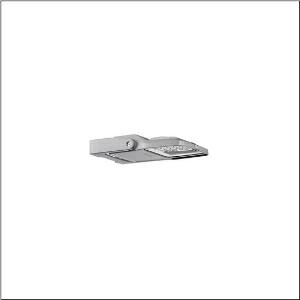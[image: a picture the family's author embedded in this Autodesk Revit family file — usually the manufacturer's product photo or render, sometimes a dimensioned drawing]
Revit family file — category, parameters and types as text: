
# Revit family: floodlight_fl_21_iq_micro___pl52_5xa7761a4d2a_29c7
name_source: partatom
category: Lighting Fixtures
units: mm (PartAtom-declared; Revit-internal decimal feet)

## family parameters
Cut with Voids When Loaded = No
Host = Face
Light Source = No
Part Type = Normal
Room Calculation Point = No
Round Connector Dimension = Use Diameter
Shared = No

## types (1)
- --- (1 x LED, 3010 lm, 23.1 W, 4000K)
    Apparent Load = 23 VA
    CIE Flux Codes = 26 60 98 100 100
    Color Rendering = 70
    Color Temperature = 4000K
    Default Elevation = 1800 mm
    Description = Floodlight FL 21 iQ micro, floodlight, primary light control with lens, of PMMA, primary optical cover: protective disc, of toughened safety glass, transparent, light distribution: PL52, light emission: direct distribution, installation type: surface-mounted, LED, High Power LED, rated luminous flux: 3.010lm, luminous efficacy: 130lm/W, light colour: 740, colour temperature: 4000K, control: optimised constant luminous flux control (CLO 2.0), Desk-Remote (wireless, voltage-free reading and setting of iQ features in the workshop via application-optimized NFC function/RFID function), Light-Fading, Smart-Wire, Night-Set, Lumen-Switch, Temp-Guard, Auto-Match, with terminal, 6-pole, mains connection: 220..240V, AC, 50/60Hz, start of lifetime: 23W, end of service life: 24W, reduction: 11W, luminaire housing, of diecast aluminium, powder-coated, Siteco® metallic grey (DB 702S), corrosivity category C5 mid according to DIN EN ISO 12944, sealing non-destructively replaceable, design bracket, of diecast aluminium, powder-coated, Siteco® metallic grey (DB 702S), protection rating (complete): IP66, insulation class (complete): insulation class II (safety insulation), certification: CE, ENEC, VDE, protection symbol: D, impact resistance: IK07, permissible operating ambient temperature: -40..+40°C, permissible operating ambient temperature for outdoor applications: -40..+50°C, standard: DIN EN 12944, LABS conformity tested according to VDMA 24364:2018-05, packaging unit: 1 piece

Light Distribution: PL52
    Height = 65 mm
    Lamp = 1 x LED
    Lamp Light Flux = 3010 lm
    Lamp Power = 23.1 W
    Lamp count = 1
    Length = 312 mm
    Luminous efficacy = 130 lm/W
    Manufacturer = Siteco
    ModVariant = No
    Model = 5XA7761A4D2A
    Mounting Place = Wall
    Mounting Type = Surface mounted
    Number of Poles = 1
    OnlyDefault = Yes
    Power Factor = 1
    Product Name = Floodlight FL 21 iQ micro | PL52
    Product group = floodlight | wall mounted
    ProductGroupID = 2001
    Protection Class = Protection class II
    Protection Degree = IP 66
    RLX_Detail_Level = 1
    RLX_Emergency_Light_Flux = 0 lm
    RLX_Emergency_Type = 0
    RLX_Emergency_Type_DB = No
    RlxData = <blob elided: 97537 chars, md5=d1d93428>
    Socket = socket
    Standby Power = 0 W
    System Light Flux = 3010 lm
    System Power = 23 W
    Type Comments = factory setting: luminous flux: 100 % | dim-lin: 254 | 455 mA
    Type Image = l_1006878.jpg
    URL = http://relux.com
    VarID = @adj_129211
    Voltage = 0 V
    Weight = 0.00 kg
    Width = 230 mm

## geometry (parser evidence)
native form markers: Blend x4, Sweep x13
no freeform markers — native parametric forms only
